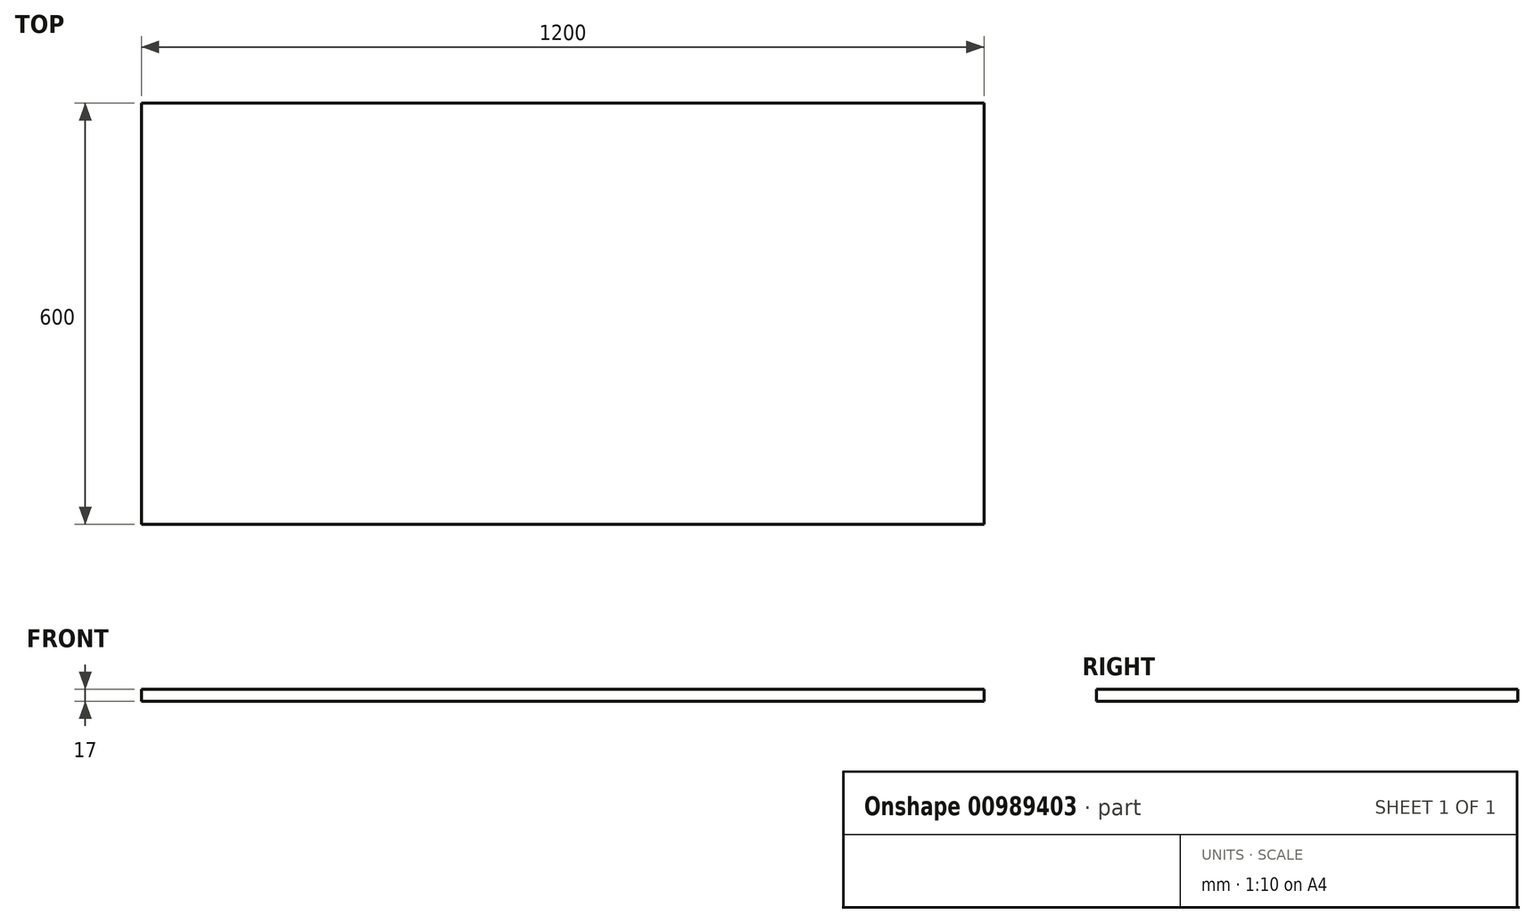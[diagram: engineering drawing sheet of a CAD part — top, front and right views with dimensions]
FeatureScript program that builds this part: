
annotation { "Feature Type Name" : "Feature", "Feature Type Description" : "" }
export const myFeature = defineFeature(function(context is Context, id is Id, definition is map)
    precondition{}
    {
        {
            var Q0;
            Q0=qCreatedBy(makeId("Top.planeOp"),FACE);
            var sketch = newSketch(context, id + "F0", { "sketchPlane" : qUnion([Q0])});
            skLineSegment(sketch, "E0.bottom", {"start": v(522.54, -259.24) * mm, "end": v(-677.46, -259.24) * mm});
            skLineSegment(sketch, "E0.top", {"start": v(522.54, 340.76) * mm, "end": v(-677.46, 340.76) * mm});
            skLineSegment(sketch, "E0.left", {"start": v(522.54, -259.24) * mm, "end": v(522.54, 340.76) * mm});
            skLineSegment(sketch, "E0.right", {"start": v(-677.46, -259.24) * mm, "end": v(-677.46, 340.76) * mm});
            skPoint(sketch, "E0.middle", {"position": v(-77.46, 40.76) * mm});
            skSolve(sketch);
        }
        {
            var Q0;
            Q0 = qSketchRegion(id + "F0", true);
            var Q1;
            Q1=makeQuery(id+"F0.imprint","IMPRINT",FACE,{"disambiguationData":[TD([[makeQuery(id+"F0.imprint","IMPRINT",EDGE,{"derivedFrom":sQuery(id+"F0.wireOp",EDGE,"E0.bottom")}),-1.0]])]});
            extrude(context, id + "F1", {"entities" : qUnion([Q0, Q1]), "depth" : 17 * mm, "offsetDistance" : 25 * mm});
        }
    });
